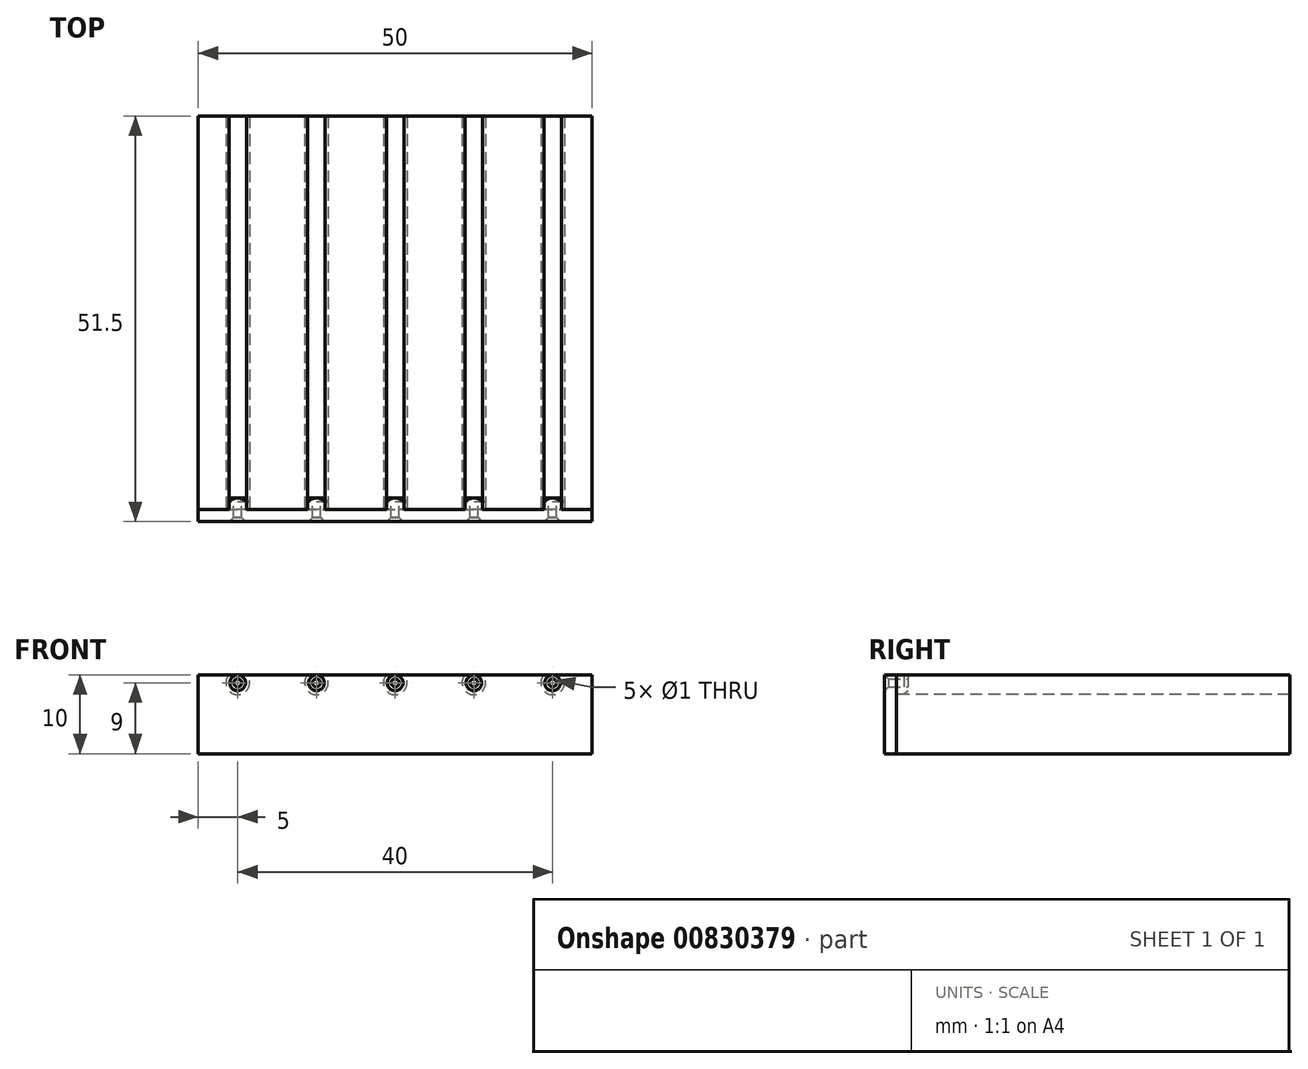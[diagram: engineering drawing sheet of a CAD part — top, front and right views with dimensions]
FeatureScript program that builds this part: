
annotation { "Feature Type Name" : "Feature", "Feature Type Description" : "" }
export const myFeature = defineFeature(function(context is Context, id is Id, definition is map)
    precondition{}
    {
        {
            var Q0;
            Q0=qCreatedBy(makeId("Top.planeOp"),FACE);
            var sketch = newSketch(context, id + "F0", { "sketchPlane" : qUnion([Q0])});
            skLineSegment(sketch, "E0.bottom", {"start": v(25, 25) * mm, "end": v(-25, 25) * mm});
            skLineSegment(sketch, "E0.top", {"start": v(25, -25) * mm, "end": v(-25, -25) * mm});
            skLineSegment(sketch, "E0.left", {"start": v(25, 25) * mm, "end": v(25, -25) * mm});
            skLineSegment(sketch, "E0.right", {"start": v(-25, 25) * mm, "end": v(-25, -25) * mm});
            skPoint(sketch, "E0.middle", {"position": v(0, 0) * mm});
            skLineSegment(sketch, "E1.bottom", {"start": v(-25, -23.5) * mm, "end": v(25, -23.5) * mm});
            skLineSegment(sketch, "E1.top", {"start": v(-25, -26.5) * mm, "end": v(25, -26.5) * mm});
            skLineSegment(sketch, "E1.left", {"start": v(-25, -23.5) * mm, "end": v(-25, -26.5) * mm});
            skLineSegment(sketch, "E1.right", {"start": v(25, -23.5) * mm, "end": v(25, -26.5) * mm});
            skSolve(sketch);
        }
        {
            var Q0;
            Q0=makeQuery(id+"F0.imprint","IMPRINT",FACE,{"disambiguationData":[TD([[makeQuery(id+"F0.imprint","IMPRINT",EDGE,{"derivedFrom":sQuery(id+"F0.wireOp",EDGE,"E0.bottom")}),1.0]])]});
            var Q1;
            {var subQ0=sQuery(id+"F0.wireOp",EDGE,"E0.top");Q1=makeQuery(id+"F0.imprint","IMPRINT",FACE,{"disambiguationData":[TD([[makeQuery(id+"F0.imprint","IMPRINT",EDGE,{"derivedFrom":subQ0}),-1.0]])]});}
            extrude(context, id + "F1", {"entities" : qUnion([Q0, Q1]), "depth" : 10 * mm, "offsetDistance" : 25 * mm});
        }
        {
            var Q0;
            Q0=makeQuery(id+"F1.opExtrude","SWEPT_FACE",FACE,{"disambiguationData":[OSD([sQuery(id+"F0.wireOp",EDGE,"E0.top")])]});
            var sketch = newSketch(context, id + "F2", { "sketchPlane" : qUnion([Q0])});
            skLineSegment(sketch, "E2.0.0", {"start": v(-25, 0) * mm, "end": v(25, 0) * mm});
            skLineSegment(sketch, "E2.0.1", {"start": v(25, 0) * mm, "end": v(25, 10) * mm});
            skLineSegment(sketch, "E2.0.2", {"start": v(25, 10) * mm, "end": v(-25, 10) * mm});
            skLineSegment(sketch, "E2.0.3", {"start": v(-25, 10) * mm, "end": v(-25, 0) * mm});
            skLineSegment(sketch, "E3", {"start": v(-25, 9) * mm, "end": v(25, 9) * mm, "construction": true});
            skCircle(sketch, "E4", {"center": v(-20, 9) * mm, "radius": 1.5 * mm});
            skCircle(sketch, "E5.1.0.0", {"center": v(-10, 9) * mm, "radius": 1.5 * mm});
            skCircle(sketch, "E5.2.0.0", {"center": v(0, 9) * mm, "radius": 1.5 * mm});
            skCircle(sketch, "E5.3.0.0", {"center": v(10, 9) * mm, "radius": 1.5 * mm});
            skLineSegment(sketch, "E5.direction1", {"start": v(-20, 9) * mm, "end": v(-10, 9) * mm, "construction": true});
            skLineSegment(sketch, "E6", {"start": v(0, 10) * mm, "end": v(0, 0) * mm, "construction": true});
            skCircle(sketch, "E7.0.4.0", {"center": v(20, 9) * mm, "radius": 1.5 * mm});
            skSolve(sketch);
        }
        {
            var Q0;
            {var subQ0=sQuery(id+"F2.wireOp",EDGE,"E5.5.0.0");var subQ1=sQuery(id+"F2.wireOp",EDGE,"E2.0.2");var subQ2=makeQuery(id+"F2.imprint","INTERSECT",VERTEX,{"disambiguationData":[OD(0.0)],"derivedFrom":[subQ1,subQ0]});Q0=makeQuery(id+"F2.imprint","IMPRINT",FACE,{"disambiguationData":[TD([[makeQuery(id+"F2.imprint","IMPRINT",EDGE,{"disambiguationData":[TD([[subQ2,-1.0]])],"derivedFrom":subQ1}),-1.0]])]});}
            var Q1;
            {var subQ0=sQuery(id+"F2.wireOp",EDGE,"E5.4.0.0");var subQ1=sQuery(id+"F2.wireOp",EDGE,"E2.0.2");var subQ2=makeQuery(id+"F2.imprint","INTERSECT",VERTEX,{"disambiguationData":[OD(0.0)],"derivedFrom":[subQ1,subQ0]});Q1=makeQuery(id+"F2.imprint","IMPRINT",FACE,{"disambiguationData":[TD([[makeQuery(id+"F2.imprint","IMPRINT",EDGE,{"disambiguationData":[TD([[subQ2,-1.0]])],"derivedFrom":subQ1}),-1.0]])]});}
            var Q2;
            {var subQ0=sQuery(id+"F2.wireOp",EDGE,"E5.3.0.0");var subQ1=sQuery(id+"F2.wireOp",EDGE,"E2.0.2");var subQ2=makeQuery(id+"F2.imprint","INTERSECT",VERTEX,{"disambiguationData":[OD(0.0)],"derivedFrom":[subQ1,subQ0]});Q2=makeQuery(id+"F2.imprint","IMPRINT",FACE,{"disambiguationData":[TD([[makeQuery(id+"F2.imprint","IMPRINT",EDGE,{"disambiguationData":[TD([[subQ2,-1.0]])],"derivedFrom":subQ1}),-1.0]])]});}
            var Q3;
            {var subQ0=sQuery(id+"F2.wireOp",EDGE,"E5.2.0.0");var subQ1=sQuery(id+"F2.wireOp",EDGE,"E2.0.2");var subQ2=makeQuery(id+"F2.imprint","INTERSECT",VERTEX,{"disambiguationData":[OD(0.0)],"derivedFrom":[subQ1,subQ0]});Q3=makeQuery(id+"F2.imprint","IMPRINT",FACE,{"disambiguationData":[TD([[makeQuery(id+"F2.imprint","IMPRINT",EDGE,{"disambiguationData":[TD([[subQ2,-1.0]])],"derivedFrom":subQ1}),-1.0]])]});}
            var Q4;
            {var subQ0=sQuery(id+"F2.wireOp",EDGE,"E5.1.0.0");var subQ1=sQuery(id+"F2.wireOp",EDGE,"E2.0.2");var subQ2=makeQuery(id+"F2.imprint","INTERSECT",VERTEX,{"disambiguationData":[OD(0.0)],"derivedFrom":[subQ1,subQ0]});Q4=makeQuery(id+"F2.imprint","IMPRINT",FACE,{"disambiguationData":[TD([[makeQuery(id+"F2.imprint","IMPRINT",EDGE,{"disambiguationData":[TD([[subQ2,-1.0]])],"derivedFrom":subQ1}),-1.0]])]});}
            var Q5;
            {var subQ0=sQuery(id+"F2.wireOp",EDGE,"E4");var subQ1=sQuery(id+"F2.wireOp",EDGE,"E2.0.2");var subQ2=makeQuery(id+"F2.imprint","INTERSECT",VERTEX,{"disambiguationData":[OD(0.0)],"derivedFrom":[subQ1,subQ0]});Q5=makeQuery(id+"F2.imprint","IMPRINT",FACE,{"disambiguationData":[TD([[makeQuery(id+"F2.imprint","IMPRINT",EDGE,{"disambiguationData":[TD([[subQ2,-1.0]])],"derivedFrom":subQ1}),-1.0]])]});}
            var Q6;
            {var subQ0=sQuery(id+"F2.wireOp",EDGE,"E5.5.0.0");var subQ1=sQuery(id+"F2.wireOp",EDGE,"E2.0.2");var subQ2=makeQuery(id+"F2.imprint","INTERSECT",VERTEX,{"disambiguationData":[OD(0.0)],"derivedFrom":[subQ1,subQ0]});Q6=makeQuery(id+"F2.imprint","IMPRINT",FACE,{"disambiguationData":[TD([[makeQuery(id+"F2.imprint","IMPRINT",EDGE,{"disambiguationData":[TD([[subQ2,-1.0]])],"derivedFrom":subQ1}),1.0]])]});}
            var Q7;
            {var subQ0=sQuery(id+"F2.wireOp",EDGE,"E5.4.0.0");var subQ1=sQuery(id+"F2.wireOp",EDGE,"E2.0.2");var subQ2=makeQuery(id+"F2.imprint","INTERSECT",VERTEX,{"disambiguationData":[OD(0.0)],"derivedFrom":[subQ1,subQ0]});Q7=makeQuery(id+"F2.imprint","IMPRINT",FACE,{"disambiguationData":[TD([[makeQuery(id+"F2.imprint","IMPRINT",EDGE,{"disambiguationData":[TD([[subQ2,-1.0]])],"derivedFrom":subQ1}),1.0]])]});}
            var Q8;
            {var subQ0=sQuery(id+"F2.wireOp",EDGE,"E5.3.0.0");var subQ1=sQuery(id+"F2.wireOp",EDGE,"E2.0.2");var subQ2=makeQuery(id+"F2.imprint","INTERSECT",VERTEX,{"disambiguationData":[OD(0.0)],"derivedFrom":[subQ1,subQ0]});Q8=makeQuery(id+"F2.imprint","IMPRINT",FACE,{"disambiguationData":[TD([[makeQuery(id+"F2.imprint","IMPRINT",EDGE,{"disambiguationData":[TD([[subQ2,-1.0]])],"derivedFrom":subQ1}),1.0]])]});}
            var Q9;
            {var subQ0=sQuery(id+"F2.wireOp",EDGE,"E5.2.0.0");var subQ1=sQuery(id+"F2.wireOp",EDGE,"E2.0.2");var subQ2=makeQuery(id+"F2.imprint","INTERSECT",VERTEX,{"disambiguationData":[OD(0.0)],"derivedFrom":[subQ1,subQ0]});Q9=makeQuery(id+"F2.imprint","IMPRINT",FACE,{"disambiguationData":[TD([[makeQuery(id+"F2.imprint","IMPRINT",EDGE,{"disambiguationData":[TD([[subQ2,-1.0]])],"derivedFrom":subQ1}),1.0]])]});}
            var Q10;
            {var subQ0=sQuery(id+"F2.wireOp",EDGE,"E5.1.0.0");var subQ1=sQuery(id+"F2.wireOp",EDGE,"E2.0.2");var subQ2=makeQuery(id+"F2.imprint","INTERSECT",VERTEX,{"disambiguationData":[OD(0.0)],"derivedFrom":[subQ1,subQ0]});Q10=makeQuery(id+"F2.imprint","IMPRINT",FACE,{"disambiguationData":[TD([[makeQuery(id+"F2.imprint","IMPRINT",EDGE,{"disambiguationData":[TD([[subQ2,-1.0]])],"derivedFrom":subQ1}),1.0]])]});}
            var Q11;
            {var subQ0=sQuery(id+"F2.wireOp",EDGE,"E4");var subQ1=sQuery(id+"F2.wireOp",EDGE,"E2.0.2");var subQ2=makeQuery(id+"F2.imprint","INTERSECT",VERTEX,{"disambiguationData":[OD(0.0)],"derivedFrom":[subQ1,subQ0]});Q11=makeQuery(id+"F2.imprint","IMPRINT",FACE,{"disambiguationData":[TD([[makeQuery(id+"F2.imprint","IMPRINT",EDGE,{"disambiguationData":[TD([[subQ2,-1.0]])],"derivedFrom":subQ1}),1.0]])]});}
            var Q12;
            {var subQ0=sQuery(id+"F2.wireOp",EDGE,"E7.0.4.0");var subQ1=sQuery(id+"F2.wireOp",EDGE,"E2.0.2");var subQ2=makeQuery(id+"F2.imprint","INTERSECT",VERTEX,{"disambiguationData":[OD(0.0)],"derivedFrom":[subQ1,subQ0]});Q12=makeQuery(id+"F2.imprint","IMPRINT",FACE,{"disambiguationData":[TD([[makeQuery(id+"F2.imprint","IMPRINT",EDGE,{"disambiguationData":[TD([[subQ2,-1.0]])],"derivedFrom":subQ1}),1.0]])]});}
            extrude(context, id + "F3", {"entities" : qUnion([Q0, Q1, Q2, Q3, Q4, Q5, Q6, Q7, Q8, Q9, Q10, Q11, Q12]), "operationType" : NewBodyOperationType.REMOVE, "endBound" : BoundingType.THROUGH_ALL, "oppositeDirection" : true, "depth" : 25 * mm, "offsetDistance" : 25 * mm});
        }
        {
            var Q0;
            {var subQ0=sQuery(id+"F0.wireOp",EDGE,"E0.top");Q0=makeQuery(id+"F0.imprint","IMPRINT",FACE,{"disambiguationData":[TD([[makeQuery(id+"F0.imprint","IMPRINT",EDGE,{"derivedFrom":subQ0}),-1.0]])]});}
            var Q1;
            {var subQ0=sQuery(id+"F0.wireOp",EDGE,"E0.top");Q1=makeQuery(id+"F0.imprint","IMPRINT",FACE,{"disambiguationData":[TD([[makeQuery(id+"F0.imprint","IMPRINT",EDGE,{"derivedFrom":subQ0}),1.0]])]});}
            extrude(context, id + "F4", {"entities" : qUnion([Q0, Q1]), "depth" : 10 * mm, "offsetDistance" : 25 * mm});
        }
        {
            var Q0;
            Q0=makeQuery(id+"F1.opExtrude","SWEPT_BODY",BODY,{"disambiguationData":[OSD([sQuery(id+"F0.wireOp",EDGE,"E0.bottom"),sQuery(id+"F0.wireOp",EDGE,"E0.top"),sQuery(id+"F0.wireOp",EDGE,"E0.left"),sQuery(id+"F0.wireOp",EDGE,"E0.right"),sQuery(id+"F0.wireOp",EDGE,"E1.left"),sQuery(id+"F0.wireOp",EDGE,"E1.right")])]});
            var Q1;
            Q1=makeQuery(id+"F4.opExtrude","SWEPT_BODY",BODY,{"disambiguationData":[OSD([sQuery(id+"F0.wireOp",EDGE,"E1.bottom"),sQuery(id+"F0.wireOp",EDGE,"E1.top"),sQuery(id+"F0.wireOp",EDGE,"E1.left"),sQuery(id+"F0.wireOp",EDGE,"E1.right")])]});
            booleanBodies(context, id + "F5", {"operationType" : BooleanOperationType.SUBTRACTION, "tools" : qUnion([Q0]), "targets" : qUnion([Q1]), "keepTools" : true});
        }
        {
            var Q0;
            {var subQ0=sQuery(id+"F0.wireOp",EDGE,"E1.bottom");Q0=makeQuery(id+"F5.opBoolean","SPLIT",FACE,{"disambiguationData":[TD([makeQuery(id+"F3.boolean.opBoolean","COPY",FACE,{"derivedFrom":makeQuery(id+"F3.opExtrude","SWEPT_FACE",FACE,{"disambiguationData":[OSD([sQuery(id+"F2.wireOp",EDGE,"E4")])]})})])],"derivedFrom":makeQuery(id+"F4.opExtrude","SWEPT_FACE",FACE,{"disambiguationData":[OSD([subQ0])]})});}
            var sketch = newSketch(context, id + "F6", { "sketchPlane" : qUnion([Q0])});
            skCircle(sketch, "E8", {"center": v(20, 9) * mm, "radius": 0.5 * mm});
            skCircle(sketch, "E9.1.0.0", {"center": v(10, 9) * mm, "radius": 0.5 * mm});
            skCircle(sketch, "E9.2.0.0", {"center": v(0, 9) * mm, "radius": 0.5 * mm});
            skCircle(sketch, "E9.3.0.0", {"center": v(-10, 9) * mm, "radius": 0.5 * mm});
            skCircle(sketch, "E9.4.0.0", {"center": v(-20, 9) * mm, "radius": 0.5 * mm});
            skLineSegment(sketch, "E9.direction1", {"start": v(20, 9) * mm, "end": v(10, 9) * mm, "construction": true});
            skSolve(sketch);
        }
        {
            var Q0;
            Q0=makeQuery(id+"F6.imprint","IMPRINT",FACE,{"disambiguationData":[TD([[makeQuery(id+"F6.imprint","IMPRINT",EDGE,{"derivedFrom":sQuery(id+"F6.wireOp",EDGE,"E8")}),1.0]])]});
            var Q1;
            Q1=makeQuery(id+"F6.imprint","IMPRINT",FACE,{"disambiguationData":[TD([[makeQuery(id+"F6.imprint","IMPRINT",EDGE,{"derivedFrom":sQuery(id+"F6.wireOp",EDGE,"E9.1.0.0")}),1.0]])]});
            var Q2;
            Q2=makeQuery(id+"F6.imprint","IMPRINT",FACE,{"disambiguationData":[TD([[makeQuery(id+"F6.imprint","IMPRINT",EDGE,{"derivedFrom":sQuery(id+"F6.wireOp",EDGE,"E9.2.0.0")}),1.0]])]});
            var Q3;
            Q3=makeQuery(id+"F6.imprint","IMPRINT",FACE,{"disambiguationData":[TD([[makeQuery(id+"F6.imprint","IMPRINT",EDGE,{"derivedFrom":sQuery(id+"F6.wireOp",EDGE,"E9.3.0.0")}),1.0]])]});
            var Q4;
            Q4=makeQuery(id+"F6.imprint","IMPRINT",FACE,{"disambiguationData":[TD([[makeQuery(id+"F6.imprint","IMPRINT",EDGE,{"derivedFrom":sQuery(id+"F6.wireOp",EDGE,"E9.4.0.0")}),1.0]])]});
            extrude(context, id + "F7", {"entities" : qUnion([Q0, Q1, Q2, Q3, Q4]), "operationType" : NewBodyOperationType.REMOVE, "oppositeDirection" : true, "depth" : 25 * mm, "offsetDistance" : 25 * mm});
        }
        {
            var Q0;
            Q0=makeQuery(id+"F5.opBoolean","INTERSECT",EDGE,{"derivedFrom":[makeQuery(id+"F3.boolean.opBoolean","COPY",FACE,{"derivedFrom":makeQuery(id+"F3.opExtrude","SWEPT_FACE",FACE,{"disambiguationData":[OSD([sQuery(id+"F2.wireOp",EDGE,"E4")])]})}),makeQuery(id+"F4.opExtrude","SWEPT_FACE",FACE,{"disambiguationData":[OSD([sQuery(id+"F0.wireOp",EDGE,"E1.bottom")])]})]});
            var Q1;
            Q1=makeQuery(id+"F5.opBoolean","INTERSECT",EDGE,{"derivedFrom":[makeQuery(id+"F3.boolean.opBoolean","COPY",FACE,{"derivedFrom":makeQuery(id+"F3.opExtrude","SWEPT_FACE",FACE,{"disambiguationData":[OSD([sQuery(id+"F2.wireOp",EDGE,"E5.1.0.0")])]})}),makeQuery(id+"F4.opExtrude","SWEPT_FACE",FACE,{"disambiguationData":[OSD([sQuery(id+"F0.wireOp",EDGE,"E1.bottom")])]})]});
            var Q2;
            Q2=makeQuery(id+"F5.opBoolean","INTERSECT",EDGE,{"derivedFrom":[makeQuery(id+"F3.boolean.opBoolean","COPY",FACE,{"derivedFrom":makeQuery(id+"F3.opExtrude","SWEPT_FACE",FACE,{"disambiguationData":[OSD([sQuery(id+"F2.wireOp",EDGE,"E5.2.0.0")])]})}),makeQuery(id+"F4.opExtrude","SWEPT_FACE",FACE,{"disambiguationData":[OSD([sQuery(id+"F0.wireOp",EDGE,"E1.bottom")])]})]});
            var Q3;
            Q3=makeQuery(id+"F7.boolean.opBoolean","INTERSECT",EDGE,{"derivedFrom":[makeQuery(id+"F4.opExtrude","SWEPT_FACE",FACE,{"disambiguationData":[OSD([sQuery(id+"F0.wireOp",EDGE,"E1.top")])]}),makeQuery(id+"F7.opExtrude","SWEPT_FACE",FACE,{"disambiguationData":[OSD([sQuery(id+"F6.wireOp",EDGE,"E9.1.0.0")])]})]});
            var Q4;
            Q4=makeQuery(id+"F7.boolean.opBoolean","INTERSECT",EDGE,{"derivedFrom":[makeQuery(id+"F4.opExtrude","SWEPT_FACE",FACE,{"disambiguationData":[OSD([sQuery(id+"F0.wireOp",EDGE,"E1.top")])]}),makeQuery(id+"F7.opExtrude","SWEPT_FACE",FACE,{"disambiguationData":[OSD([sQuery(id+"F6.wireOp",EDGE,"E8")])]})]});
            var Q5;
            Q5=makeQuery(id+"F7.boolean.opBoolean","INTERSECT",EDGE,{"derivedFrom":[makeQuery(id+"F4.opExtrude","SWEPT_FACE",FACE,{"disambiguationData":[OSD([sQuery(id+"F0.wireOp",EDGE,"E1.top")])]}),makeQuery(id+"F7.opExtrude","SWEPT_FACE",FACE,{"disambiguationData":[OSD([sQuery(id+"F6.wireOp",EDGE,"E9.2.0.0")])]})]});
            var Q6;
            Q6=makeQuery(id+"F7.boolean.opBoolean","INTERSECT",EDGE,{"derivedFrom":[makeQuery(id+"F4.opExtrude","SWEPT_FACE",FACE,{"disambiguationData":[OSD([sQuery(id+"F0.wireOp",EDGE,"E1.top")])]}),makeQuery(id+"F7.opExtrude","SWEPT_FACE",FACE,{"disambiguationData":[OSD([sQuery(id+"F6.wireOp",EDGE,"E9.3.0.0")])]})]});
            var Q7;
            Q7=makeQuery(id+"F7.boolean.opBoolean","INTERSECT",EDGE,{"derivedFrom":[makeQuery(id+"F4.opExtrude","SWEPT_FACE",FACE,{"disambiguationData":[OSD([sQuery(id+"F0.wireOp",EDGE,"E1.top")])]}),makeQuery(id+"F7.opExtrude","SWEPT_FACE",FACE,{"disambiguationData":[OSD([sQuery(id+"F6.wireOp",EDGE,"E9.4.0.0")])]})]});
            var Q8;
            Q8=makeQuery(id+"F5.opBoolean","INTERSECT",EDGE,{"derivedFrom":[makeQuery(id+"F3.boolean.opBoolean","COPY",FACE,{"derivedFrom":makeQuery(id+"F3.opExtrude","SWEPT_FACE",FACE,{"disambiguationData":[OSD([sQuery(id+"F2.wireOp",EDGE,"E5.3.0.0")])]})}),makeQuery(id+"F4.opExtrude","SWEPT_FACE",FACE,{"disambiguationData":[OSD([sQuery(id+"F0.wireOp",EDGE,"E1.bottom")])]})]});
            var Q9;
            Q9=makeQuery(id+"F5.opBoolean","INTERSECT",EDGE,{"derivedFrom":[makeQuery(id+"F3.boolean.opBoolean","COPY",FACE,{"derivedFrom":makeQuery(id+"F3.opExtrude","SWEPT_FACE",FACE,{"disambiguationData":[OSD([sQuery(id+"F2.wireOp",EDGE,"E7.0.4.0")])]})}),makeQuery(id+"F4.opExtrude","SWEPT_FACE",FACE,{"disambiguationData":[OSD([sQuery(id+"F0.wireOp",EDGE,"E1.bottom")])]})]});
            chamfer(context, id + "F8", {"entities" : qUnion([Q0, Q1, Q2, Q3, Q4, Q5, Q6, Q7, Q8, Q9]), "width" : .5 * mm, "tangentPropagation" : true});
        }
    });
